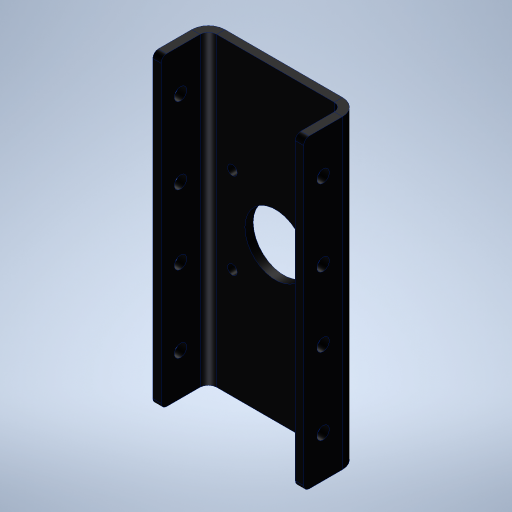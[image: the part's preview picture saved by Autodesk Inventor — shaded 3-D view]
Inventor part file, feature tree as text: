
AUTODESK INVENTOR PART (.ipt)
format: ipt  version: 2024 (Build 280153000, 153)  size: 406,016 bytes
history: native  units: mm
features: other x9, sketch x6, extrude x4, fillet x1
ambient origin geometry x8: Origin, YZ Plane, XZ Plane, XY Plane, X Axis, Y Axis, Z Axis, Center Point
bodies: Volumenkörper1 (feature_tree)
feature tree (20):
  extrude  "Extrusion1"  Depth=42.3mm
  extrude  "Extrusion2"  Depth=3.0mm
  extrude  "Extrusion3"  Depth=15.5mm
  other  "Lasche1"
  other  "Lasche2"
  sketch  "Skizze6"  dims[d14=3.0mm d15=3.0mm d16=1.5mm d17=6.0mm d18=3.0mm d19=20.0mm d20=90.0deg d21=3.0mm d22=12.0mm d23=3.0mm d24=3.0mm d25=3.0mm d26=1.5mm d27=6.0mm d28=3.0mm d29=20.0mm d30=90.0deg d31=3.0mm d32=12.0mm d33=3.0mm d34=3.0mm d35=4.5mm d36=4.5mm d37=25.0mm d40=2.0mm d41=4.5mm d42=4.5mm d43=80.0mm d44=100.0mm d45=0.0mm d46=0.5mm d47=0.872665mm d48=0.5mm d49=0.872665mm]
  fillet  "Rundung2"  Radius=31.0mm
  extrude  "Extrusion5"  Depth=3.5mm
  sketch  "Skizze1"  dims[d0=110.0mm d1=42.3mm]
  sketch  "Skizze2"  dims[d2=3.0mm d3=0.0mm d4=22.0mm]
  sketch  "Skizze3"  dims[d5=4.0mm d6=0.0mm d7=15.5mm d8=31.0mm]
  sketch  "Skizze4"  dims[d9=3.5mm d10=3.5mm]
  other  "Grobblech1"
  other  "Biegung1"
  other  "Ecke1"
  sketch  "Skizze5"  dims[d11=4.0mm d12=0.0mm]
  other  "Grobblech2"
  other  "Biegung2"
  other  "Ecke2"
  other  "Definition1"
